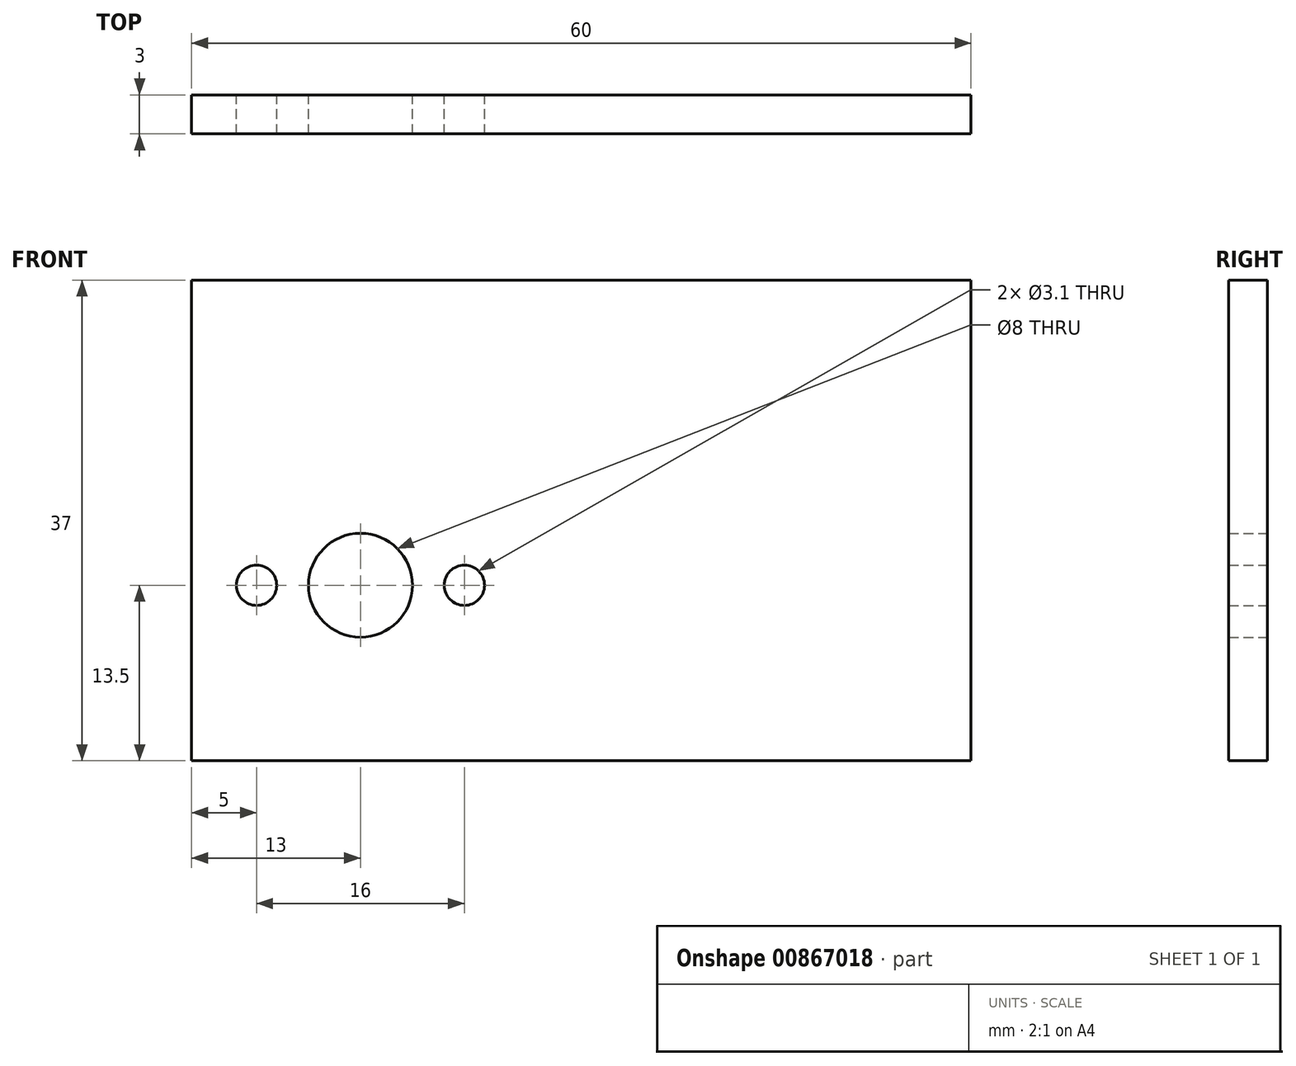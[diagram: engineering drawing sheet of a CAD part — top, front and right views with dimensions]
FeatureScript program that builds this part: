
annotation { "Feature Type Name" : "Feature", "Feature Type Description" : "" }
export const myFeature = defineFeature(function(context is Context, id is Id, definition is map)
    precondition{}
    {
        {
            var Q0;
            Q0=qCreatedBy(makeId("Front.planeOp"),FACE);
            var sketch = newSketch(context, id + "F0", { "sketchPlane" : qUnion([Q0])});
            skLineSegment(sketch, "E0.bottom", {"start": v(-13, -13.5) * mm, "end": v(47, -13.5) * mm});
            skLineSegment(sketch, "E0.top", {"start": v(-13, 23.5) * mm, "end": v(47, 23.5) * mm});
            skLineSegment(sketch, "E0.left", {"start": v(-13, -13.5) * mm, "end": v(-13, 23.5) * mm});
            skLineSegment(sketch, "E0.right", {"start": v(47, -13.5) * mm, "end": v(47, 23.5) * mm});
            skCircle(sketch, "E1", {"center": v(0, 0) * mm, "radius": 4 * mm});
            skCircle(sketch, "E2", {"center": v(-8, 0) * mm, "radius": 1.55 * mm});
            skCircle(sketch, "E3.MirrorC", {"center": v(8, 0) * mm, "radius": 1.55 * mm});
            skSolve(sketch);
        }
        {
            var Q0;
            Q0 = qSketchRegion(id + "F0", true);
            extrude(context, id + "F1", {"entities" : qUnion([Q0]), "depth" : 3 * mm, "offsetDistance" : 25 * mm});
        }
    });
